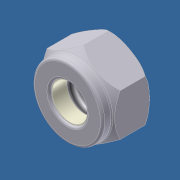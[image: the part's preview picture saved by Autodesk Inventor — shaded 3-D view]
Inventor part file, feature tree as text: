
AUTODESK INVENTOR PART (.ipt)
format: ipt  version: 2012 (Build 160160000, 160)  size: 159,744 bytes
history: native  units: in
note: dims shown in document units (in); Inventor stores cm internally (conversion verified against a paired STEP export)
features: revolve x3, sketch x2, extrude x1, hole x1, fillet x1, projected_geometry x1
ambient origin geometry x8: Origin, YZ Plane, XZ Plane, XY Plane, X Axis, Y Axis, Z Axis, Center Point
bodies: Solid1 (feature_tree)
feature tree (9):
  extrude  "Extrusion1"  Depth=0.309in TaperAngle=0.0deg
  sketch  "Sketch2"  dims[d3=0.11in d4=45.0deg d5=0.24in d6=0.12in d7=0.015in d8=0.1in d9=0.1in d10=90.0deg d11=0.25in d12=0.03in d13=0.1in d14=90.0deg d15=1.0in d16=1.0in d17=0.252in d18=0.5in d19=0.375in d20=0.25in d21=0.5635in d22=0.75in d23=0.8108in d24=0.015in d25=90.0deg]
  revolve  "Revolution1"  Angle=45.0deg
  revolve  "Revolution2"  [1 undecoded]
  hole  "Hole1"  [1 undecoded]
  fillet  "Fillet1"  Radius=0.015in
  revolve  "Revolution3"  [1 undecoded]
  sketch  "Sketch1"  dims[d0=0.5in d1=0.309in d2=0.0in]
  projected_geometry  "Projected Loop1"
note: 3 required parameter values undecoded (feature->parameter linkage not recoverable at this tier; creation-order binding heuristic only, values carry confidence <= 0.55)